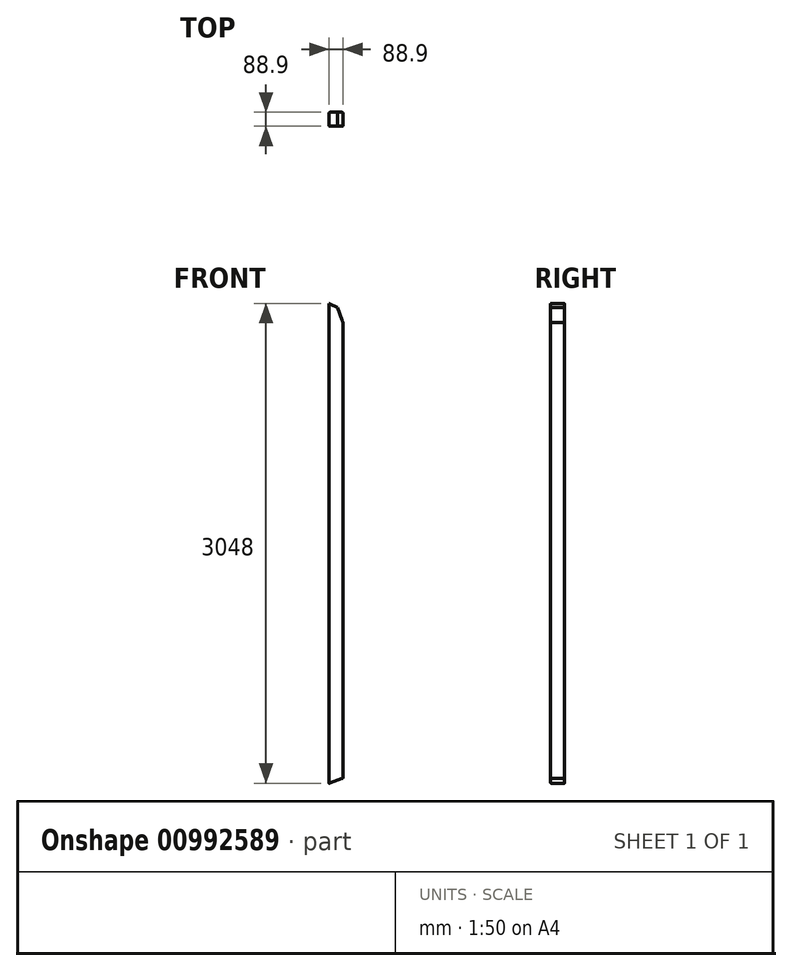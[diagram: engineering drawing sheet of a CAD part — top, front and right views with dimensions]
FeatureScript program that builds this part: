
annotation { "Feature Type Name" : "Feature", "Feature Type Description" : "" }
export const myFeature = defineFeature(function(context is Context, id is Id, definition is map)
    precondition{}
    {
        {
            var Q0;
            Q0=qCreatedBy(makeId("Top.planeOp"),FACE);
            var sketch = newSketch(context, id + "F0", { "sketchPlane" : qUnion([Q0])});
            skLineSegment(sketch, "E0.bottom", {"start": v(-44.45, 44.45) * mm, "end": v(44.45, 44.45) * mm});
            skLineSegment(sketch, "E0.top", {"start": v(-44.45, -44.45) * mm, "end": v(44.45, -44.45) * mm});
            skLineSegment(sketch, "E0.left", {"start": v(-44.45, 44.45) * mm, "end": v(-44.45, -44.45) * mm});
            skLineSegment(sketch, "E0.right", {"start": v(44.45, 44.45) * mm, "end": v(44.45, -44.45) * mm});
            skSolve(sketch);
        }
        {
            var Q0;
            Q0 = qSketchRegion(id + "F0", true);
            extrude(context, id + "F1", {"entities" : qUnion([Q0]), "depth" : 3048 * mm, "offsetDistance" : 25.4 * mm});
        }
        {
            var Q0;
            Q0=qCreatedBy(makeId("Front.planeOp"),FACE);
            var sketch = newSketch(context, id + "F2", { "sketchPlane" : qUnion([Q0])});
            skLineSegment(sketch, "E1.0", {"start": v(-44.45, 3048) * mm, "end": v(44.45, 3048) * mm});
            skLineSegment(sketch, "E2.0", {"start": v(44.45, 3048) * mm, "end": v(44.45, 0) * mm});
            skLineSegment(sketch, "E3", {"start": v(0, 3048) * mm, "end": v(44.45, 2925.87) * mm});
            skSolve(sketch);
        }
        {
            var Q0;
            Q0 = qSketchRegion(id + "F2", true);
            extrude(context, id + "F3", {"entities" : qUnion([Q0]), "operationType" : NewBodyOperationType.REMOVE, "endBound" : BoundingType.THROUGH_ALL, "depth" : 25.4 * mm, "offsetDistance" : 25.4 * mm, "hasSecondDirection" : true, "secondDirectionBound" : BoundingType.THROUGH_ALL, "secondDirectionOppositeDirection" : true, "secondDirectionDepth" : 25.4 * mm});
        }
        {
            var Q0;
            Q0=qCreatedBy(makeId("Front.planeOp"),FACE);
            var sketch = newSketch(context, id + "F4", { "sketchPlane" : qUnion([Q0])});
            skLineSegment(sketch, "E4.0", {"start": v(44.45, 2925.87) * mm, "end": v(44.45, 0) * mm});
            skLineSegment(sketch, "E5.0", {"start": v(-44.45, 0) * mm, "end": v(44.45, 0) * mm});
            skLineSegment(sketch, "E6", {"start": v(-44.45, 0) * mm, "end": v(44.45, 32.36) * mm});
            skSolve(sketch);
        }
        {
            var Q0;
            Q0 = qSketchRegion(id + "F4", true);
            extrude(context, id + "F5", {"entities" : qUnion([Q0]), "operationType" : NewBodyOperationType.REMOVE, "endBound" : BoundingType.THROUGH_ALL, "oppositeDirection" : true, "depth" : 25.4 * mm, "offsetDistance" : 25.4 * mm, "hasSecondDirection" : true, "secondDirectionBound" : BoundingType.THROUGH_ALL, "secondDirectionOppositeDirection" : false, "secondDirectionDepth" : 25.4 * mm});
        }
        {
            var Q0;
            Q0=makeQuery(id+"F1.opExtrude","SWEPT_FACE",FACE,{"disambiguationData":[OSD([sQuery(id+"F0.wireOp",EDGE,"E0.top")])]});
            var sketch = newSketch(context, id + "F6", { "sketchPlane" : qUnion([Q0])});
            skLineSegment(sketch, "E7.0", {"start": v(-44.45, 3048) * mm, "end": v(0, 3048) * mm});
            skLineSegment(sketch, "E8.0", {"start": v(0, 3048) * mm, "end": v(44.45, 2925.87) * mm});
            skLineSegment(sketch, "E9", {"start": v(-44.45, 3048) * mm, "end": v(9.09, 3023.04) * mm});
            skSolve(sketch);
        }
        {
            var Q0;
            {var subQ0=sQuery(id+"F6.wireOp",EDGE,"E7.0");Q0=makeQuery(id+"F6.imprint","IMPRINT",FACE,{"disambiguationData":[TD([[makeQuery(id+"F6.imprint","IMPRINT",EDGE,{"derivedFrom":subQ0}),-1.0]])]});}
            extrude(context, id + "F7", {"entities" : qUnion([Q0]), "operationType" : NewBodyOperationType.REMOVE, "endBound" : BoundingType.THROUGH_ALL, "oppositeDirection" : true, "depth" : 25.4 * mm, "offsetDistance" : 25.4 * mm});
        }
        {
            var Q0;
            Q0=makeQuery(id+"F1.opExtrude","SWEPT_EDGE",EDGE,{"disambiguationData":[OSD([sQuery(id+"F0.wireOp",EDGE,"E0.top"),sQuery(id+"F0.wireOp",EDGE,"E0.left")])]});
            var Q1;
            Q1=makeQuery(id+"F1.opExtrude","SWEPT_EDGE",EDGE,{"disambiguationData":[OSD([sQuery(id+"F0.wireOp",EDGE,"E0.top"),sQuery(id+"F0.wireOp",EDGE,"E0.right")])]});
            var Q2;
            Q2=makeQuery(id+"F1.opExtrude","SWEPT_EDGE",EDGE,{"disambiguationData":[OSD([sQuery(id+"F0.wireOp",EDGE,"E0.bottom"),sQuery(id+"F0.wireOp",EDGE,"E0.right")])]});
            var Q3;
            Q3=makeQuery(id+"F1.opExtrude","SWEPT_EDGE",EDGE,{"disambiguationData":[OSD([sQuery(id+"F0.wireOp",EDGE,"E0.bottom"),sQuery(id+"F0.wireOp",EDGE,"E0.left")])]});
            fillet(context, id + "F8", {"entities" : qUnion([Q0, Q1, Q2, Q3]), "radius" : 6.35 * mm, "tangentPropagation" : true, "allowEdgeOverflow" : false});
        }
    });
